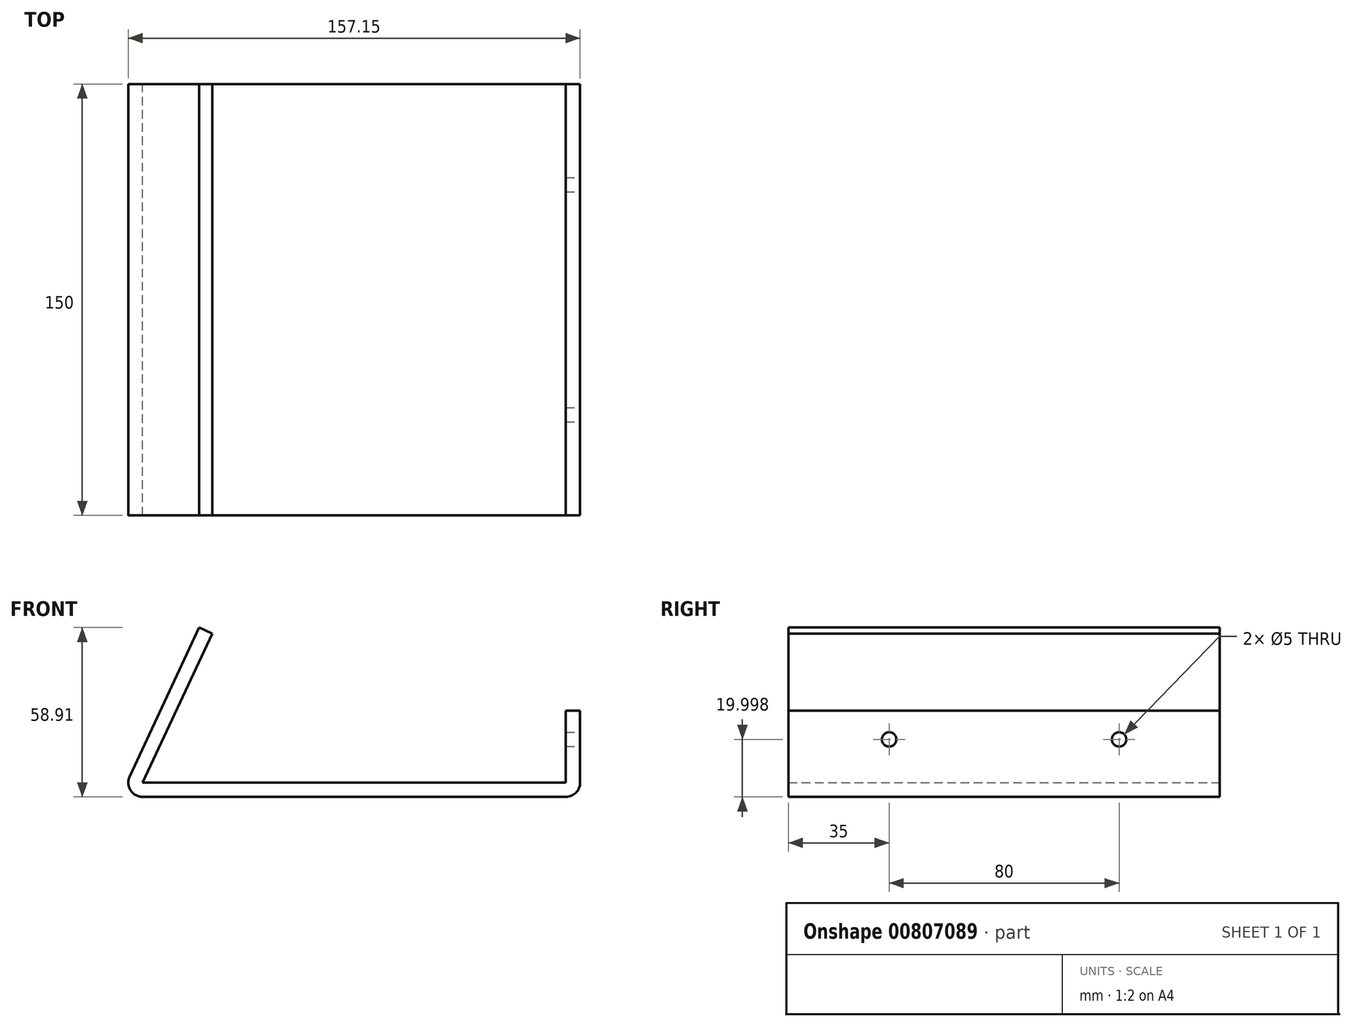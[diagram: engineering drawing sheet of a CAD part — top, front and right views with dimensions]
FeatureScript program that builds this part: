
annotation { "Feature Type Name" : "Feature", "Feature Type Description" : "" }
export const myFeature = defineFeature(function(context is Context, id is Id, definition is map)
    precondition{}
    {
        {
            var Q0;
            Q0=qCreatedBy(makeId("Front.planeOp"),FACE);
            var sketch = newSketch(context, id + "F0", { "sketchPlane" : qUnion([Q0])});
            skLineSegment(sketch, "E0", {"start": v(-75, -23.3) * mm, "end": v(85, -23.3) * mm});
            skLineSegment(sketch, "E1", {"start": v(-75, -23.3) * mm, "end": v(-47.54, 35.6) * mm});
            skLineSegment(sketch, "E2", {"start": v(85, -23.3) * mm, "end": v(85, 6.7) * mm});
            skLineSegment(sketch, "E3.0", {"start": v(-67.16, -18.3) * mm, "end": v(-43, 33.5) * mm});
            skLineSegment(sketch, "E3.1", {"start": v(-67.16, -18.3) * mm, "end": v(80, -18.3) * mm});
            skLineSegment(sketch, "E3.2", {"start": v(80, -18.3) * mm, "end": v(80, 6.7) * mm});
            skLineSegment(sketch, "E4", {"start": v(-47.54, 35.6) * mm, "end": v(-43, 33.5) * mm});
            skLineSegment(sketch, "E5", {"start": v(80, 6.7) * mm, "end": v(85, 6.7) * mm});
            skSolve(sketch);
        }
        {
            var Q0;
            Q0 = qSketchRegion(id + "F0", true);
            extrude(context, id + "F1", {"entities" : qUnion([Q0]), "depth" : 150 * mm, "offsetDistance" : 25 * mm});
        }
        {
            var Q0;
            Q0=makeQuery(id+"F1.opExtrude","SWEPT_EDGE",EDGE,{"disambiguationData":[OSD([sQuery(id+"F0.wireOp",EDGE,"E0"),sQuery(id+"F0.wireOp",EDGE,"E1")])]});
            var Q1;
            Q1=makeQuery(id+"F1.opExtrude","SWEPT_EDGE",EDGE,{"disambiguationData":[OSD([sQuery(id+"F0.wireOp",EDGE,"E0"),sQuery(id+"F0.wireOp",EDGE,"E2")])]});
            fillet(context, id + "F2", {"entities" : qUnion([Q0, Q1]), "radius" : 5 * mm, "tangentPropagation" : true, "allowEdgeOverflow" : false});
        }
        {
            var Q0;
            Q0=makeQuery(id+"F1.opExtrude","SWEPT_FACE",FACE,{"disambiguationData":[OSD([sQuery(id+"F0.wireOp",EDGE,"E2")])]});
            var sketch = newSketch(context, id + "F3", { "sketchPlane" : qUnion([Q0])});
            skLineSegment(sketch, "E6", {"start": v(-167.38, -3.3) * mm, "end": v(27.67, -3.3) * mm, "construction": true});
            skCircle(sketch, "E7", {"center": v(-115, -3.3) * mm, "radius": 2.5 * mm});
            skCircle(sketch, "E8", {"center": v(-35, -3.3) * mm, "radius": 2.5 * mm});
            skSolve(sketch);
        }
        {
            var Q0;
            Q0 = qSketchRegion(id + "F3", true);
            extrude(context, id + "F4", {"entities" : qUnion([Q0]), "operationType" : NewBodyOperationType.REMOVE, "oppositeDirection" : true, "depth" : 25 * mm, "offsetDistance" : 25 * mm});
        }
    });
